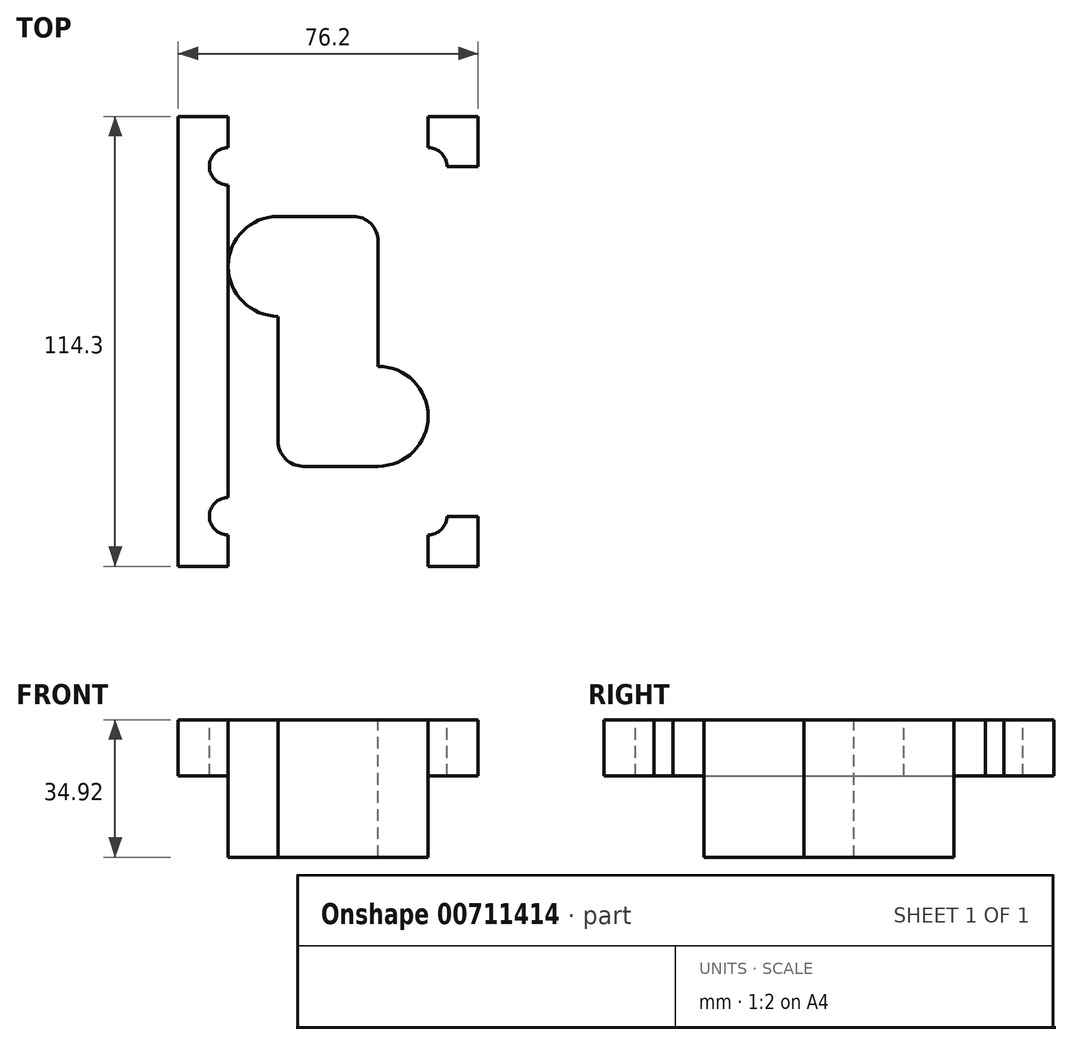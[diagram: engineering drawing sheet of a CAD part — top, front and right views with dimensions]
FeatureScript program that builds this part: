
annotation { "Feature Type Name" : "Feature", "Feature Type Description" : "" }
export const myFeature = defineFeature(function(context is Context, id is Id, definition is map)
    precondition{}
    {
        {
            var Q0;
            Q0=qCreatedBy(makeId("Top.planeOp"),FACE);
            var sketch = newSketch(context, id + "F0", { "sketchPlane" : qUnion([Q0])});
            skLineSegment(sketch, "E0.bottom", {"start": v(12.7, -31.75) * mm, "end": v(-6.35, -31.75) * mm});
            skLineSegment(sketch, "E0.top", {"start": v(6.35, 31.75) * mm, "end": v(-12.7, 31.75) * mm});
            skLineSegment(sketch, "E0.right", {"start": v(-12.7, -25.4) * mm, "end": v(-12.7, 6.35) * mm});
            skPoint(sketch, "E0.middle", {"position": v(0, 0) * mm});
            skArc(sketch, "E1", {"start": v(-12.7, 31.75) * mm, "mid": v(-25.4, 19.05) * mm, "end": v(-12.7, 6.35) * mm});
            skArc(sketch, "E2", {"start": v(12.7, -31.75) * mm, "mid": v(25.4, -19.05) * mm, "end": v(12.7, -6.35) * mm});
            skLineSegment(sketch, "E3.trimOffspring", {"start": v(12.7, -6.35) * mm, "end": v(12.7, 25.4) * mm});
            skPoint(sketch, "E4.visualSharp", {"position": v(-12.7, -31.75) * mm});
            skArc(sketch, "E4.filletArc", {"start": v(-12.7, -25.4) * mm, "mid": v(-10.84, -29.9) * mm, "end": v(-6.35, -31.75) * mm});
            skPoint(sketch, "E5.visualSharp", {"position": v(12.7, 31.75) * mm});
            skArc(sketch, "E5.filletArc", {"start": v(12.7, 25.4) * mm, "mid": v(10.84, 29.9) * mm, "end": v(6.35, 31.75) * mm});
            skLineSegment(sketch, "E6.bottom", {"start": v(0, -19.05) * mm, "end": v(-6.35, -19.05) * mm});
            skLineSegment(sketch, "E6.top", {"start": v(0, 19.05) * mm, "end": v(-6.35, 19.05) * mm});
            skLineSegment(sketch, "E6.left", {"start": v(6.35, -12.7) * mm, "end": v(6.35, 12.7) * mm});
            skLineSegment(sketch, "E6.right", {"start": v(-6.35, -19.05) * mm, "end": v(-6.35, 19.05) * mm});
            skPoint(sketch, "E7.visualSharp", {"position": v(6.35, 19.05) * mm});
            skArc(sketch, "E7.filletArc", {"start": v(6.35, 12.7) * mm, "mid": v(4.5, 17.2) * mm, "end": v(0, 19.05) * mm});
            skPoint(sketch, "E8.visualSharp", {"position": v(6.35, -19.05) * mm});
            skArc(sketch, "E8.filletArc", {"start": v(0, -19.05) * mm, "mid": v(4.5, -17.2) * mm, "end": v(6.35, -12.7) * mm});
            skLineSegment(sketch, "E9.bottom", {"start": v(38.1, -57.15) * mm, "end": v(-38.1, -57.15) * mm});
            skLineSegment(sketch, "E9.top", {"start": v(38.1, 57.15) * mm, "end": v(-38.1, 57.15) * mm});
            skLineSegment(sketch, "E9.left", {"start": v(38.1, -57.15) * mm, "end": v(38.1, 57.15) * mm});
            skLineSegment(sketch, "E9.right", {"start": v(-38.1, -57.15) * mm, "end": v(-38.1, 57.15) * mm});
            skLineSegment(sketch, "E10", {"start": v(-38.1, 44.45) * mm, "end": v(38.1, 44.45) * mm});
            skLineSegment(sketch, "E11", {"start": v(38.1, 44.45) * mm, "end": v(38.1, -44.45) * mm});
            skLineSegment(sketch, "E12", {"start": v(38.1, -44.45) * mm, "end": v(-38.1, -44.45) * mm});
            skLineSegment(sketch, "E13", {"start": v(-25.4, 57.15) * mm, "end": v(-25.4, -57.15) * mm});
            skLineSegment(sketch, "E14", {"start": v(25.4, -57.15) * mm, "end": v(25.4, 57.15) * mm});
            skCircle(sketch, "E15", {"center": v(-25.4, 44.45) * mm, "radius": 4.76 * mm});
            skCircle(sketch, "E16", {"center": v(25.4, 44.45) * mm, "radius": 4.76 * mm});
            skCircle(sketch, "E17", {"center": v(25.4, -44.45) * mm, "radius": 4.76 * mm});
            skCircle(sketch, "E18", {"center": v(-25.4, -44.45) * mm, "radius": 4.76 * mm});
            skSolve(sketch);
        }
        {
            var Q0;
            {var subQ0=sQuery(id+"F0.wireOp",EDGE,"E14");var subQ1=sQuery(id+"F0.wireOp",EDGE,"E10");var subQ2=makeQuery(id+"F0.imprint","INTERSECT",VERTEX,{"derivedFrom":[subQ1,subQ0]});Q0=makeQuery(id+"F0.imprint","IMPRINT",FACE,{"disambiguationData":[TD([[makeQuery(id+"F0.imprint","IMPRINT",EDGE,{"disambiguationData":[TD([[subQ2,-1.0]])],"derivedFrom":subQ1}),1.0]])]});}
            var Q1;
            {var subQ0=sQuery(id+"F0.wireOp",EDGE,"E17");var subQ1=sQuery(id+"F0.wireOp",EDGE,"E12");var subQ2=makeQuery(id+"F0.imprint","INTERSECT",VERTEX,{"disambiguationData":[OD(0.0)],"derivedFrom":[subQ1,subQ0]});Q1=makeQuery(id+"F0.imprint","IMPRINT",FACE,{"disambiguationData":[TD([[makeQuery(id+"F0.imprint","IMPRINT",EDGE,{"disambiguationData":[TD([[subQ2,-1.0]])],"derivedFrom":subQ1}),1.0]])]});}
            var Q2;
            {var subQ0=sQuery(id+"F0.wireOp",EDGE,"E17");var subQ1=sQuery(id+"F0.wireOp",EDGE,"E12");var subQ2=makeQuery(id+"F0.imprint","INTERSECT",VERTEX,{"disambiguationData":[OD(0.0)],"derivedFrom":[subQ1,subQ0]});Q2=makeQuery(id+"F0.imprint","IMPRINT",FACE,{"disambiguationData":[TD([[makeQuery(id+"F0.imprint","IMPRINT",EDGE,{"disambiguationData":[TD([[subQ2,-1.0]])],"derivedFrom":subQ1}),-1.0]])]});}
            var Q3;
            {var subQ0=sQuery(id+"F0.wireOp",EDGE,"E18");var subQ1=sQuery(id+"F0.wireOp",EDGE,"E12");var subQ2=makeQuery(id+"F0.imprint","INTERSECT",VERTEX,{"disambiguationData":[OD(0.0)],"derivedFrom":[subQ1,subQ0]});Q3=makeQuery(id+"F0.imprint","IMPRINT",FACE,{"disambiguationData":[TD([[makeQuery(id+"F0.imprint","IMPRINT",EDGE,{"disambiguationData":[TD([[subQ2,-1.0]])],"derivedFrom":subQ1}),-1.0]])]});}
            var Q4;
            {var subQ0=sQuery(id+"F0.wireOp",EDGE,"E18");var subQ1=sQuery(id+"F0.wireOp",EDGE,"E12");var subQ2=makeQuery(id+"F0.imprint","INTERSECT",VERTEX,{"disambiguationData":[OD(0.0)],"derivedFrom":[subQ1,subQ0]});Q4=makeQuery(id+"F0.imprint","IMPRINT",FACE,{"disambiguationData":[TD([[makeQuery(id+"F0.imprint","IMPRINT",EDGE,{"disambiguationData":[TD([[subQ2,-1.0]])],"derivedFrom":subQ1}),1.0]])]});}
            var Q5;
            {var subQ0=sQuery(id+"F0.wireOp",EDGE,"E16");var subQ1=sQuery(id+"F0.wireOp",EDGE,"E10");var subQ2=makeQuery(id+"F0.imprint","INTERSECT",VERTEX,{"disambiguationData":[OD(0.0)],"derivedFrom":[subQ1,subQ0]});Q5=makeQuery(id+"F0.imprint","IMPRINT",FACE,{"disambiguationData":[TD([[makeQuery(id+"F0.imprint","IMPRINT",EDGE,{"disambiguationData":[TD([[subQ2,-1.0]])],"derivedFrom":subQ1}),1.0]])]});}
            var Q6;
            {var subQ1=sQuery(id+"F0.wireOp",EDGE,"E9.top");var subQ5=sQuery(id+"F0.wireOp",EDGE,"E13");var subQ6=makeQuery(id+"F0.imprint","INTERSECT",VERTEX,{"derivedFrom":[subQ1,subQ5]});Q6=makeQuery(id+"F0.imprint","IMPRINT",FACE,{"disambiguationData":[TD([[makeQuery(id+"F0.imprint","IMPRINT",EDGE,{"disambiguationData":[TD([[subQ6,1.0]])],"derivedFrom":subQ1}),1.0]])]});}
            var Q7;
            {var subQ0=sQuery(id+"F0.wireOp",EDGE,"E13");var subQ1=sQuery(id+"F0.wireOp",EDGE,"E12");var subQ2=makeQuery(id+"F0.imprint","INTERSECT",VERTEX,{"derivedFrom":[subQ1,subQ0]});Q7=makeQuery(id+"F0.imprint","IMPRINT",FACE,{"disambiguationData":[TD([[makeQuery(id+"F0.imprint","IMPRINT",EDGE,{"disambiguationData":[TD([[subQ2,-1.0]])],"derivedFrom":subQ1}),-1.0]])]});}
            var Q8;
            {var subQ0=sQuery(id+"F0.wireOp",EDGE,"E14");var subQ1=sQuery(id+"F0.wireOp",EDGE,"E10");var subQ2=makeQuery(id+"F0.imprint","INTERSECT",VERTEX,{"derivedFrom":[subQ1,subQ0]});Q8=makeQuery(id+"F0.imprint","IMPRINT",FACE,{"disambiguationData":[TD([[makeQuery(id+"F0.imprint","IMPRINT",EDGE,{"disambiguationData":[TD([[subQ2,-1.0]])],"derivedFrom":subQ1}),-1.0]])]});}
            var Q9;
            {var subQ0=sQuery(id+"F0.wireOp",EDGE,"E13");var subQ1=sQuery(id+"F0.wireOp",EDGE,"E10");var subQ2=makeQuery(id+"F0.imprint","INTERSECT",VERTEX,{"derivedFrom":[subQ1,subQ0]});Q9=makeQuery(id+"F0.imprint","IMPRINT",FACE,{"disambiguationData":[TD([[makeQuery(id+"F0.imprint","IMPRINT",EDGE,{"disambiguationData":[TD([[subQ2,-1.0]])],"derivedFrom":subQ1}),-1.0]])]});}
            var Q10;
            {var subQ0=sQuery(id+"F0.wireOp",EDGE,"E15");var subQ1=sQuery(id+"F0.wireOp",EDGE,"E10");var subQ2=makeQuery(id+"F0.imprint","INTERSECT",VERTEX,{"disambiguationData":[OD(0.0)],"derivedFrom":[subQ1,subQ0]});Q10=makeQuery(id+"F0.imprint","IMPRINT",FACE,{"disambiguationData":[TD([[makeQuery(id+"F0.imprint","IMPRINT",EDGE,{"disambiguationData":[TD([[subQ2,-1.0]])],"derivedFrom":subQ1}),1.0]])]});}
            var Q11;
            {var subQ0=sQuery(id+"F0.wireOp",EDGE,"E13");var subQ1=sQuery(id+"F0.wireOp",EDGE,"E10");var subQ2=makeQuery(id+"F0.imprint","INTERSECT",VERTEX,{"derivedFrom":[subQ1,subQ0]});Q11=makeQuery(id+"F0.imprint","IMPRINT",FACE,{"disambiguationData":[TD([[makeQuery(id+"F0.imprint","IMPRINT",EDGE,{"disambiguationData":[TD([[subQ2,-1.0]])],"derivedFrom":subQ1}),1.0]])]});}
            var Q12;
            {var subQ0=sQuery(id+"F0.wireOp",EDGE,"E15");var subQ1=sQuery(id+"F0.wireOp",EDGE,"E10");var subQ2=makeQuery(id+"F0.imprint","INTERSECT",VERTEX,{"disambiguationData":[OD(0.0)],"derivedFrom":[subQ1,subQ0]});Q12=makeQuery(id+"F0.imprint","IMPRINT",FACE,{"disambiguationData":[TD([[makeQuery(id+"F0.imprint","IMPRINT",EDGE,{"disambiguationData":[TD([[subQ2,-1.0]])],"derivedFrom":subQ1}),-1.0]])]});}
            var Q13;
            {var subQ1=sQuery(id+"F0.wireOp",EDGE,"E11");Q13=makeQuery(id+"F0.imprint","IMPRINT",FACE,{"disambiguationData":[TD([[makeQuery(id+"F0.imprint","IMPRINT",EDGE,{"derivedFrom":subQ1}),-1.0]])]});}
            var Q14;
            {var subQ1=sQuery(id+"F0.wireOp",EDGE,"E9.top");var subQ6=sQuery(id+"F0.wireOp",EDGE,"E9.right");var subQ9=makeQuery(id+"F0.imprint","INTERSECT",VERTEX,{"derivedFrom":[subQ1,subQ6]});Q14=makeQuery(id+"F0.imprint","IMPRINT",FACE,{"disambiguationData":[TD([[makeQuery(id+"F0.imprint","IMPRINT",EDGE,{"disambiguationData":[TD([[subQ9,1.0]])],"derivedFrom":subQ1}),1.0]])]});}
            var Q15;
            {var subQ1=sQuery(id+"F0.wireOp",EDGE,"E9.top");var subQ6=sQuery(id+"F0.wireOp",EDGE,"E9.left");var subQ9=makeQuery(id+"F0.imprint","INTERSECT",VERTEX,{"derivedFrom":[subQ1,subQ6]});Q15=makeQuery(id+"F0.imprint","IMPRINT",FACE,{"disambiguationData":[TD([[makeQuery(id+"F0.imprint","IMPRINT",EDGE,{"disambiguationData":[TD([[subQ9,-1.0]])],"derivedFrom":subQ1}),1.0]])]});}
            var Q16;
            {var subQ1=sQuery(id+"F0.wireOp",EDGE,"E9.bottom");var subQ7=sQuery(id+"F0.wireOp",EDGE,"E9.right");var subQ9=makeQuery(id+"F0.imprint","INTERSECT",VERTEX,{"derivedFrom":[subQ1,subQ7]});Q16=makeQuery(id+"F0.imprint","IMPRINT",FACE,{"disambiguationData":[TD([[makeQuery(id+"F0.imprint","IMPRINT",EDGE,{"disambiguationData":[TD([[subQ9,1.0]])],"derivedFrom":subQ1}),-1.0]])]});}
            var Q17;
            {var subQ1=sQuery(id+"F0.wireOp",EDGE,"E9.left");var subQ5=sQuery(id+"F0.wireOp",EDGE,"E9.bottom");var subQ6=makeQuery(id+"F0.imprint","INTERSECT",VERTEX,{"derivedFrom":[subQ5,subQ1]});Q17=makeQuery(id+"F0.imprint","IMPRINT",FACE,{"disambiguationData":[TD([[makeQuery(id+"F0.imprint","IMPRINT",EDGE,{"disambiguationData":[TD([[subQ6,-1.0]])],"derivedFrom":subQ5}),-1.0]])]});}
            var Q18;
            {var subQ0=sQuery(id+"F0.wireOp",EDGE,"E14");var subQ1=sQuery(id+"F0.wireOp",EDGE,"E12");var subQ2=makeQuery(id+"F0.imprint","INTERSECT",VERTEX,{"derivedFrom":[subQ1,subQ0]});Q18=makeQuery(id+"F0.imprint","IMPRINT",FACE,{"disambiguationData":[TD([[makeQuery(id+"F0.imprint","IMPRINT",EDGE,{"disambiguationData":[TD([[subQ2,-1.0]])],"derivedFrom":subQ1}),1.0]])]});}
            var Q19;
            Q19=makeQuery(id+"F0.imprint","IMPRINT",FACE,{"disambiguationData":[TD([[makeQuery(id+"F0.imprint","IMPRINT",EDGE,{"derivedFrom":sQuery(id+"F0.wireOp",EDGE,"E0.bottom")}),-1.0]])]});
            var Q20;
            {var subQ1=sQuery(id+"F0.wireOp",EDGE,"E9.bottom");var subQ8=sQuery(id+"F0.wireOp",EDGE,"E13");var subQ10=makeQuery(id+"F0.imprint","INTERSECT",VERTEX,{"derivedFrom":[subQ1,subQ8]});Q20=makeQuery(id+"F0.imprint","IMPRINT",FACE,{"disambiguationData":[TD([[makeQuery(id+"F0.imprint","IMPRINT",EDGE,{"disambiguationData":[TD([[subQ10,1.0]])],"derivedFrom":subQ1}),-1.0]])]});}
            var Q21;
            Q21=makeQuery(id+"F0.imprint","IMPRINT",FACE,{"disambiguationData":[TD([[makeQuery(id+"F0.imprint","IMPRINT",EDGE,{"derivedFrom":sQuery(id+"F0.wireOp",EDGE,"E6.bottom")}),-1.0]])]});
            var Q22;
            Q22=makeQuery(id+"F0.imprint","IMPRINT",FACE,{"disambiguationData":[TD([[makeQuery(id+"F0.imprint","IMPRINT",EDGE,{"derivedFrom":sQuery(id+"F0.wireOp",EDGE,"E0.bottom")}),1.0]])]});
            var Q23;
            {var subQ0=sQuery(id+"F0.wireOp",EDGE,"E16");var subQ1=sQuery(id+"F0.wireOp",EDGE,"E10");var subQ2=makeQuery(id+"F0.imprint","INTERSECT",VERTEX,{"disambiguationData":[OD(0.0)],"derivedFrom":[subQ1,subQ0]});Q23=makeQuery(id+"F0.imprint","IMPRINT",FACE,{"disambiguationData":[TD([[makeQuery(id+"F0.imprint","IMPRINT",EDGE,{"disambiguationData":[TD([[subQ2,-1.0]])],"derivedFrom":subQ1}),-1.0]])]});}
            var Q24;
            {var subQ0=sQuery(id+"F0.wireOp",EDGE,"E14");var subQ1=sQuery(id+"F0.wireOp",EDGE,"E12");var subQ2=makeQuery(id+"F0.imprint","INTERSECT",VERTEX,{"derivedFrom":[subQ1,subQ0]});Q24=makeQuery(id+"F0.imprint","IMPRINT",FACE,{"disambiguationData":[TD([[makeQuery(id+"F0.imprint","IMPRINT",EDGE,{"disambiguationData":[TD([[subQ2,-1.0]])],"derivedFrom":subQ1}),-1.0]])]});}
            var Q25;
            {var subQ1=sQuery(id+"F0.wireOp",EDGE,"E9.right");var subQ5=sQuery(id+"F0.wireOp",EDGE,"E10");var subQ6=makeQuery(id+"F0.imprint","INTERSECT",VERTEX,{"derivedFrom":[subQ1,subQ5]});Q25=makeQuery(id+"F0.imprint","IMPRINT",FACE,{"disambiguationData":[TD([[makeQuery(id+"F0.imprint","IMPRINT",EDGE,{"disambiguationData":[TD([[subQ6,1.0]])],"derivedFrom":subQ1}),-1.0]])]});}
            var Q26;
            {var subQ0=sQuery(id+"F0.wireOp",EDGE,"E13");var subQ1=sQuery(id+"F0.wireOp",EDGE,"E12");var subQ2=makeQuery(id+"F0.imprint","INTERSECT",VERTEX,{"derivedFrom":[subQ1,subQ0]});Q26=makeQuery(id+"F0.imprint","IMPRINT",FACE,{"disambiguationData":[TD([[makeQuery(id+"F0.imprint","IMPRINT",EDGE,{"disambiguationData":[TD([[subQ2,-1.0]])],"derivedFrom":subQ1}),1.0]])]});}
            var Q27;
            Q27=sQuery(id+"F0.wireOp",EDGE,"E9.bottom");
            var Q28;
            Q28=sQuery(id+"F0.wireOp",EDGE,"E9.right");
            var Q29;
            Q29=sQuery(id+"F0.wireOp",EDGE,"E9.top");
            var Q30;
            Q30=sQuery(id+"F0.wireOp",EDGE,"E9.left");
            extrude(context, id + "F1", {"entities" : qUnion([Q0, Q1, Q2, Q3, Q4, Q5, Q6, Q7, Q8, Q9, Q10, Q11, Q12, Q13, Q14, Q15, Q16, Q17, Q18, Q19, Q20, Q21, Q22, Q23, Q24, Q25, Q26]), "surfaceEntities" : qUnion([Q27, Q28, Q29, Q30]), "depth" : -14.29 * mm, "offsetDistance" : 25.4 * mm});
        }
        {
            var Q0;
            Q0=makeQuery(id+"F0.imprint","IMPRINT",FACE,{"disambiguationData":[TD([[makeQuery(id+"F0.imprint","IMPRINT",EDGE,{"derivedFrom":sQuery(id+"F0.wireOp",EDGE,"E0.bottom")}),-1.0]])]});
            var Q1;
            Q1=makeQuery(id+"F0.imprint","IMPRINT",FACE,{"disambiguationData":[TD([[makeQuery(id+"F0.imprint","IMPRINT",EDGE,{"derivedFrom":sQuery(id+"F0.wireOp",EDGE,"E6.bottom")}),-1.0]])]});
            extrude(context, id + "F2", {"entities" : qUnion([Q0, Q1]), "operationType" : NewBodyOperationType.ADD, "depth" : -34.92 * mm, "offsetDistance" : 25.4 * mm});
        }
        {
            var Q0;
            {var subQ0=sQuery(id+"F0.wireOp",EDGE,"E15");var subQ1=sQuery(id+"F0.wireOp",EDGE,"E10");var subQ2=makeQuery(id+"F0.imprint","INTERSECT",VERTEX,{"disambiguationData":[OD(0.0)],"derivedFrom":[subQ1,subQ0]});Q0=makeQuery(id+"F0.imprint","IMPRINT",FACE,{"disambiguationData":[TD([[makeQuery(id+"F0.imprint","IMPRINT",EDGE,{"disambiguationData":[TD([[subQ2,-1.0]])],"derivedFrom":subQ1}),1.0]])]});}
            var Q1;
            {var subQ0=sQuery(id+"F0.wireOp",EDGE,"E13");var subQ1=sQuery(id+"F0.wireOp",EDGE,"E10");var subQ2=makeQuery(id+"F0.imprint","INTERSECT",VERTEX,{"derivedFrom":[subQ1,subQ0]});Q1=makeQuery(id+"F0.imprint","IMPRINT",FACE,{"disambiguationData":[TD([[makeQuery(id+"F0.imprint","IMPRINT",EDGE,{"disambiguationData":[TD([[subQ2,-1.0]])],"derivedFrom":subQ1}),1.0]])]});}
            var Q2;
            {var subQ0=sQuery(id+"F0.wireOp",EDGE,"E13");var subQ1=sQuery(id+"F0.wireOp",EDGE,"E10");var subQ2=makeQuery(id+"F0.imprint","INTERSECT",VERTEX,{"derivedFrom":[subQ1,subQ0]});Q2=makeQuery(id+"F0.imprint","IMPRINT",FACE,{"disambiguationData":[TD([[makeQuery(id+"F0.imprint","IMPRINT",EDGE,{"disambiguationData":[TD([[subQ2,-1.0]])],"derivedFrom":subQ1}),-1.0]])]});}
            var Q3;
            {var subQ0=sQuery(id+"F0.wireOp",EDGE,"E15");var subQ1=sQuery(id+"F0.wireOp",EDGE,"E10");var subQ2=makeQuery(id+"F0.imprint","INTERSECT",VERTEX,{"disambiguationData":[OD(0.0)],"derivedFrom":[subQ1,subQ0]});Q3=makeQuery(id+"F0.imprint","IMPRINT",FACE,{"disambiguationData":[TD([[makeQuery(id+"F0.imprint","IMPRINT",EDGE,{"disambiguationData":[TD([[subQ2,-1.0]])],"derivedFrom":subQ1}),-1.0]])]});}
            var Q4;
            {var subQ0=sQuery(id+"F0.wireOp",EDGE,"E14");var subQ1=sQuery(id+"F0.wireOp",EDGE,"E10");var subQ2=makeQuery(id+"F0.imprint","INTERSECT",VERTEX,{"derivedFrom":[subQ1,subQ0]});Q4=makeQuery(id+"F0.imprint","IMPRINT",FACE,{"disambiguationData":[TD([[makeQuery(id+"F0.imprint","IMPRINT",EDGE,{"disambiguationData":[TD([[subQ2,-1.0]])],"derivedFrom":subQ1}),-1.0]])]});}
            var Q5;
            {var subQ0=sQuery(id+"F0.wireOp",EDGE,"E14");var subQ1=sQuery(id+"F0.wireOp",EDGE,"E10");var subQ2=makeQuery(id+"F0.imprint","INTERSECT",VERTEX,{"derivedFrom":[subQ1,subQ0]});Q5=makeQuery(id+"F0.imprint","IMPRINT",FACE,{"disambiguationData":[TD([[makeQuery(id+"F0.imprint","IMPRINT",EDGE,{"disambiguationData":[TD([[subQ2,-1.0]])],"derivedFrom":subQ1}),1.0]])]});}
            var Q6;
            {var subQ0=sQuery(id+"F0.wireOp",EDGE,"E16");var subQ1=sQuery(id+"F0.wireOp",EDGE,"E10");var subQ2=makeQuery(id+"F0.imprint","INTERSECT",VERTEX,{"disambiguationData":[OD(0.0)],"derivedFrom":[subQ1,subQ0]});Q6=makeQuery(id+"F0.imprint","IMPRINT",FACE,{"disambiguationData":[TD([[makeQuery(id+"F0.imprint","IMPRINT",EDGE,{"disambiguationData":[TD([[subQ2,-1.0]])],"derivedFrom":subQ1}),-1.0]])]});}
            var Q7;
            {var subQ0=sQuery(id+"F0.wireOp",EDGE,"E16");var subQ1=sQuery(id+"F0.wireOp",EDGE,"E10");var subQ2=makeQuery(id+"F0.imprint","INTERSECT",VERTEX,{"disambiguationData":[OD(0.0)],"derivedFrom":[subQ1,subQ0]});Q7=makeQuery(id+"F0.imprint","IMPRINT",FACE,{"disambiguationData":[TD([[makeQuery(id+"F0.imprint","IMPRINT",EDGE,{"disambiguationData":[TD([[subQ2,-1.0]])],"derivedFrom":subQ1}),1.0]])]});}
            var Q8;
            {var subQ0=sQuery(id+"F0.wireOp",EDGE,"E18");var subQ1=sQuery(id+"F0.wireOp",EDGE,"E12");var subQ2=makeQuery(id+"F0.imprint","INTERSECT",VERTEX,{"disambiguationData":[OD(0.0)],"derivedFrom":[subQ1,subQ0]});Q8=makeQuery(id+"F0.imprint","IMPRINT",FACE,{"disambiguationData":[TD([[makeQuery(id+"F0.imprint","IMPRINT",EDGE,{"disambiguationData":[TD([[subQ2,-1.0]])],"derivedFrom":subQ1}),-1.0]])]});}
            var Q9;
            {var subQ0=sQuery(id+"F0.wireOp",EDGE,"E13");var subQ1=sQuery(id+"F0.wireOp",EDGE,"E12");var subQ2=makeQuery(id+"F0.imprint","INTERSECT",VERTEX,{"derivedFrom":[subQ1,subQ0]});Q9=makeQuery(id+"F0.imprint","IMPRINT",FACE,{"disambiguationData":[TD([[makeQuery(id+"F0.imprint","IMPRINT",EDGE,{"disambiguationData":[TD([[subQ2,-1.0]])],"derivedFrom":subQ1}),-1.0]])]});}
            var Q10;
            {var subQ0=sQuery(id+"F0.wireOp",EDGE,"E13");var subQ1=sQuery(id+"F0.wireOp",EDGE,"E12");var subQ2=makeQuery(id+"F0.imprint","INTERSECT",VERTEX,{"derivedFrom":[subQ1,subQ0]});Q10=makeQuery(id+"F0.imprint","IMPRINT",FACE,{"disambiguationData":[TD([[makeQuery(id+"F0.imprint","IMPRINT",EDGE,{"disambiguationData":[TD([[subQ2,-1.0]])],"derivedFrom":subQ1}),1.0]])]});}
            var Q11;
            {var subQ0=sQuery(id+"F0.wireOp",EDGE,"E18");var subQ1=sQuery(id+"F0.wireOp",EDGE,"E12");var subQ2=makeQuery(id+"F0.imprint","INTERSECT",VERTEX,{"disambiguationData":[OD(0.0)],"derivedFrom":[subQ1,subQ0]});Q11=makeQuery(id+"F0.imprint","IMPRINT",FACE,{"disambiguationData":[TD([[makeQuery(id+"F0.imprint","IMPRINT",EDGE,{"disambiguationData":[TD([[subQ2,-1.0]])],"derivedFrom":subQ1}),1.0]])]});}
            var Q12;
            {var subQ0=sQuery(id+"F0.wireOp",EDGE,"E14");var subQ1=sQuery(id+"F0.wireOp",EDGE,"E12");var subQ2=makeQuery(id+"F0.imprint","INTERSECT",VERTEX,{"derivedFrom":[subQ1,subQ0]});Q12=makeQuery(id+"F0.imprint","IMPRINT",FACE,{"disambiguationData":[TD([[makeQuery(id+"F0.imprint","IMPRINT",EDGE,{"disambiguationData":[TD([[subQ2,-1.0]])],"derivedFrom":subQ1}),-1.0]])]});}
            var Q13;
            {var subQ0=sQuery(id+"F0.wireOp",EDGE,"E17");var subQ1=sQuery(id+"F0.wireOp",EDGE,"E12");var subQ2=makeQuery(id+"F0.imprint","INTERSECT",VERTEX,{"disambiguationData":[OD(0.0)],"derivedFrom":[subQ1,subQ0]});Q13=makeQuery(id+"F0.imprint","IMPRINT",FACE,{"disambiguationData":[TD([[makeQuery(id+"F0.imprint","IMPRINT",EDGE,{"disambiguationData":[TD([[subQ2,-1.0]])],"derivedFrom":subQ1}),-1.0]])]});}
            var Q14;
            {var subQ0=sQuery(id+"F0.wireOp",EDGE,"E17");var subQ1=sQuery(id+"F0.wireOp",EDGE,"E12");var subQ2=makeQuery(id+"F0.imprint","INTERSECT",VERTEX,{"disambiguationData":[OD(0.0)],"derivedFrom":[subQ1,subQ0]});Q14=makeQuery(id+"F0.imprint","IMPRINT",FACE,{"disambiguationData":[TD([[makeQuery(id+"F0.imprint","IMPRINT",EDGE,{"disambiguationData":[TD([[subQ2,-1.0]])],"derivedFrom":subQ1}),1.0]])]});}
            var Q15;
            {var subQ0=sQuery(id+"F0.wireOp",EDGE,"E14");var subQ1=sQuery(id+"F0.wireOp",EDGE,"E12");var subQ2=makeQuery(id+"F0.imprint","INTERSECT",VERTEX,{"derivedFrom":[subQ1,subQ0]});Q15=makeQuery(id+"F0.imprint","IMPRINT",FACE,{"disambiguationData":[TD([[makeQuery(id+"F0.imprint","IMPRINT",EDGE,{"disambiguationData":[TD([[subQ2,-1.0]])],"derivedFrom":subQ1}),1.0]])]});}
            var Q16;
            Q16=makeQuery(id+"F1.opExtrude","SWEPT_FACE",FACE,{"disambiguationData":[OSD([sQuery(id+"F0.wireOp",EDGE,"E9.bottom")])]});
            extrude(context, id + "F3", {"entities" : qUnion([Q0, Q1, Q2, Q3, Q4, Q5, Q6, Q7, Q8, Q9, Q10, Q11, Q12, Q13, Q14, Q15]), "operationType" : NewBodyOperationType.REMOVE, "endBound" : BoundingType.UP_TO_NEXT, "oppositeDirection" : true, "depth" : 25.4 * mm, "endBoundEntityFace" : qUnion([Q16]), "offsetDistance" : 25.4 * mm});
        }
    });
